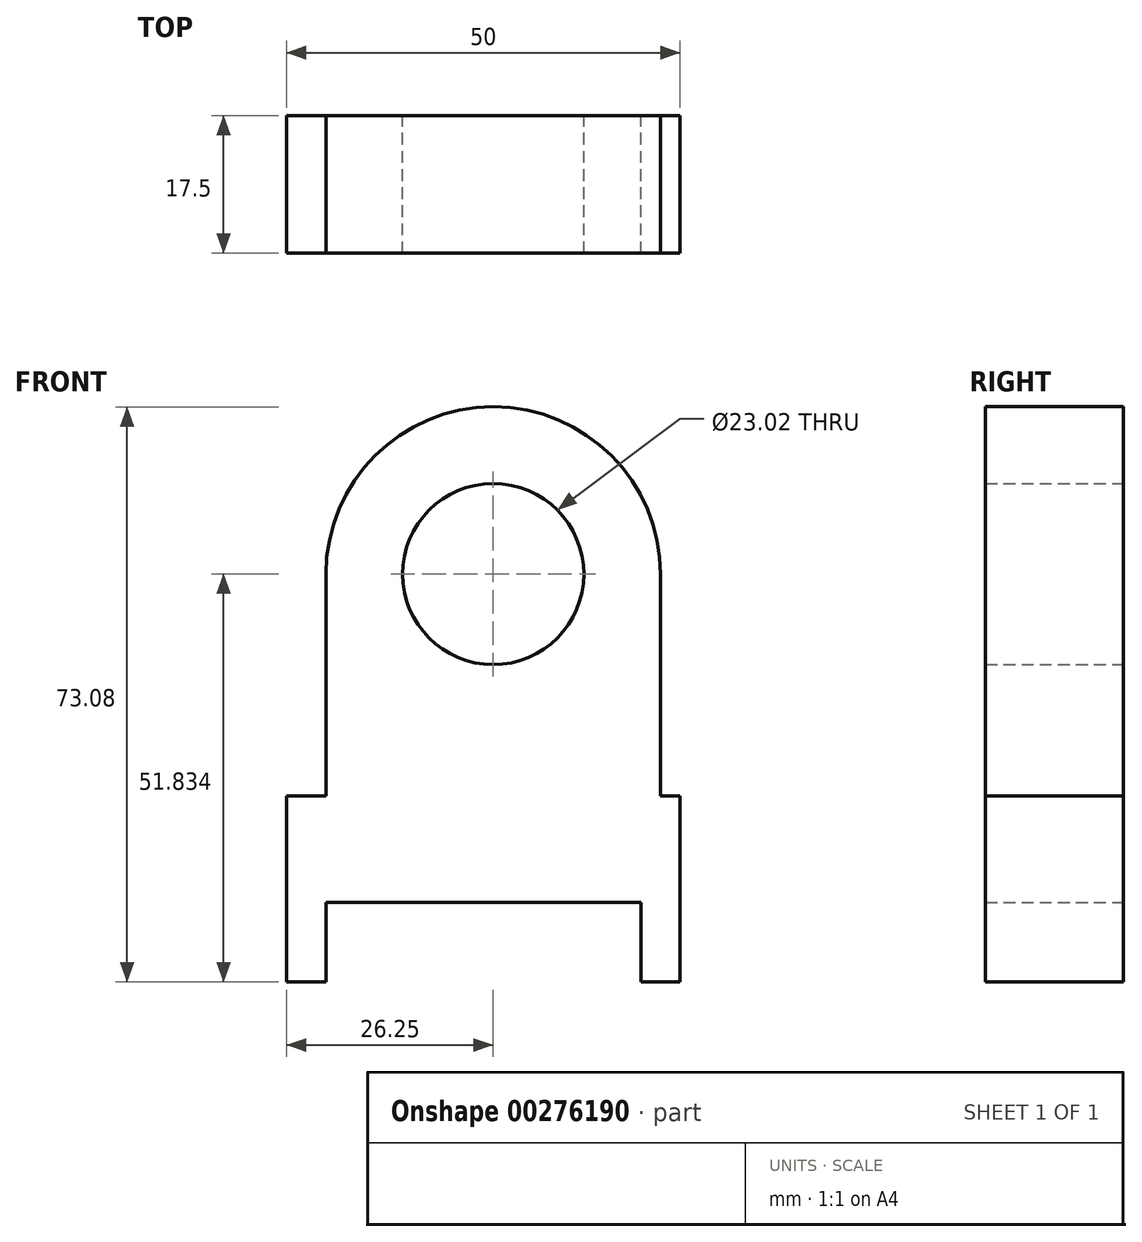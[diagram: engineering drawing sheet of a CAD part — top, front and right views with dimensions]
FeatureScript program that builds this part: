
annotation { "Feature Type Name" : "Feature", "Feature Type Description" : "" }
export const myFeature = defineFeature(function(context is Context, id is Id, definition is map)
    precondition{}
    {
        {
            var Q0;
            Q0=qCreatedBy(makeId("Front.planeOp"),FACE);
            var sketch = newSketch(context, id + "F0", { "sketchPlane" : qUnion([Q0])});
            skLineSegment(sketch, "E0", {"start": v(0, 0) * mm, "end": v(-5, 0) * mm});
            skLineSegment(sketch, "E1", {"start": v(-5, 0) * mm, "end": v(-5, 10.13) * mm});
            skLineSegment(sketch, "E2", {"start": v(-5, 10.13) * mm, "end": v(-45, 10.13) * mm});
            skLineSegment(sketch, "E3", {"start": v(-45, 10.13) * mm, "end": v(-45, 0) * mm});
            skLineSegment(sketch, "E4", {"start": v(-45, 0) * mm, "end": v(-50, 0) * mm});
            skLineSegment(sketch, "E5", {"start": v(-50, 0) * mm, "end": v(-50, 23.63) * mm});
            skLineSegment(sketch, "E6", {"start": v(-50, 23.63) * mm, "end": v(-45, 23.63) * mm});
            skLineSegment(sketch, "E7", {"start": v(-45, 23.63) * mm, "end": v(-45, 51.83) * mm});
            skLineSegment(sketch, "E8", {"start": v(-2.5, 51.83) * mm, "end": v(-2.5, 23.63) * mm});
            skLineSegment(sketch, "E9", {"start": v(-2.5, 23.63) * mm, "end": v(0, 23.63) * mm});
            skLineSegment(sketch, "E10", {"start": v(0, 23.63) * mm, "end": v(0, 0) * mm});
            skArc(sketch, "E11", {"start": v(-2.5, 51.83) * mm, "mid": v(-23.75, 73.08) * mm, "end": v(-45, 51.83) * mm});
            skCircle(sketch, "E12", {"center": v(-23.75, 51.83) * mm, "radius": 11.5 * mm});
            skSolve(sketch);
        }
        {
            var Q0;
            Q0 = qSketchRegion(id + "F0", true);
            extrude(context, id + "F1", {"entities" : qUnion([Q0]), "depth" : 17.5 * mm});
        }
    });
